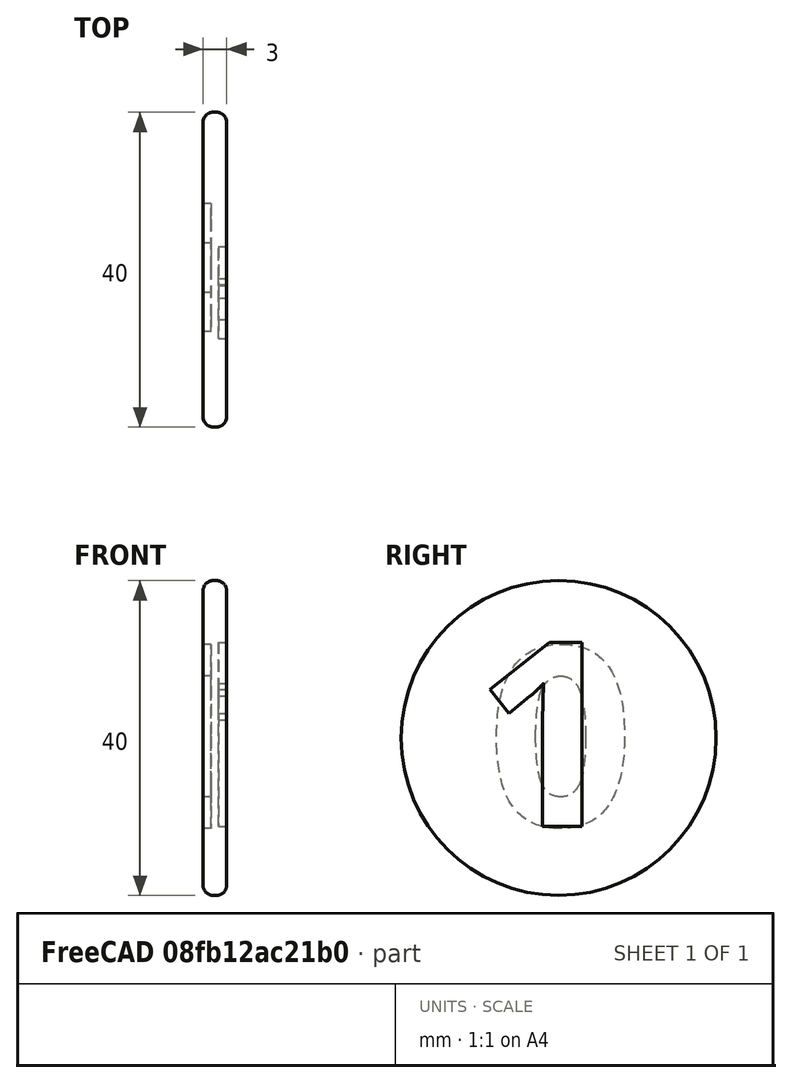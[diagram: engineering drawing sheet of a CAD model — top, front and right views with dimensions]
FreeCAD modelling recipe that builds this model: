
FCSTD DOCUMENT  (FreeCAD 0.17R12412 (Git))
Label: moneda-bit
License: All rights reserved
LicenseURL: http://en.wikipedia.org/wiki/All_rights_reserved
objects: Part::Part2DObjectPython×2, Part::Extrusion×2, Part::Cut×2, Part::Cylinder×1, Part::Fillet×1
note: 8 computed .brp shape members not serialized (recipe doc carries the construction recipe); baked Part::Feature solids carry a one-line shape summary decoded from their .brp

FEATURE [Part::Cylinder] Cylinder
  Angle = 360
  AttacherType = Attacher::AttachEngine3D
  Height = 3
  Placement = pos=(0,0,0) rot=(0,-1,0;1.5708rad)
  Radius = 20
FEATURE [Part::Part2DObjectPython] ShapeString  # Draft 2D object (typed FeaturePython)
  FontFile = <userpath>/develop/3D-parts/2017-10-10-moneda-cube/OpenSans-Bold.ttf
  Placement = pos=(-1,-10.5736,-11.2448) rot=(0.57735,0.57735,0.57735;2.0944rad)
  Size = 30
  String = 1
  Support = -> [Cylinder]
  Tracking = 0
FEATURE [Part::Extrusion] Extrude
  Base = -> ShapeString
  Dir = (1,0,0)
  DirMode = 2
  FaceMakerClass = Part::FaceMakerBullseye
  LengthFwd = 2
  LengthRev = 0
  Solid = false
  Symmetric = false
FEATURE [Part::Cut] Cut
  Base = -> Cylinder
  Tool = -> Extrude
FEATURE [Part::Part2DObjectPython] ShapeString001  # Draft 2D object (typed FeaturePython)
  FontFile = <userpath>/develop/3D-parts/2017-10-10-moneda-cube/OpenSans-Bold.ttf
  Placement = pos=(-2,9.53233,-11.5058) rot=(0.57735,-0.57735,-0.57735;2.0944rad)
  Size = 30
  String = 0
  Support = -> [Cut]
  Tracking = 0
FEATURE [Part::Extrusion] Extrude001
  Base = -> ShapeString001
  Dir = (-1,0,0)
  DirMode = 2
  FaceMakerClass = Part::FaceMakerBullseye
  LengthFwd = 2
  LengthRev = 0
  Solid = false
  Symmetric = false
FEATURE [Part::Cut] Cut001
  Base = -> Cut
  Tool = -> Extrude001
FEATURE [Part::Fillet] Fillet
  Base = -> Cut001
  Edges = 2 edges r=1.3: [Edge1,Edge3]
